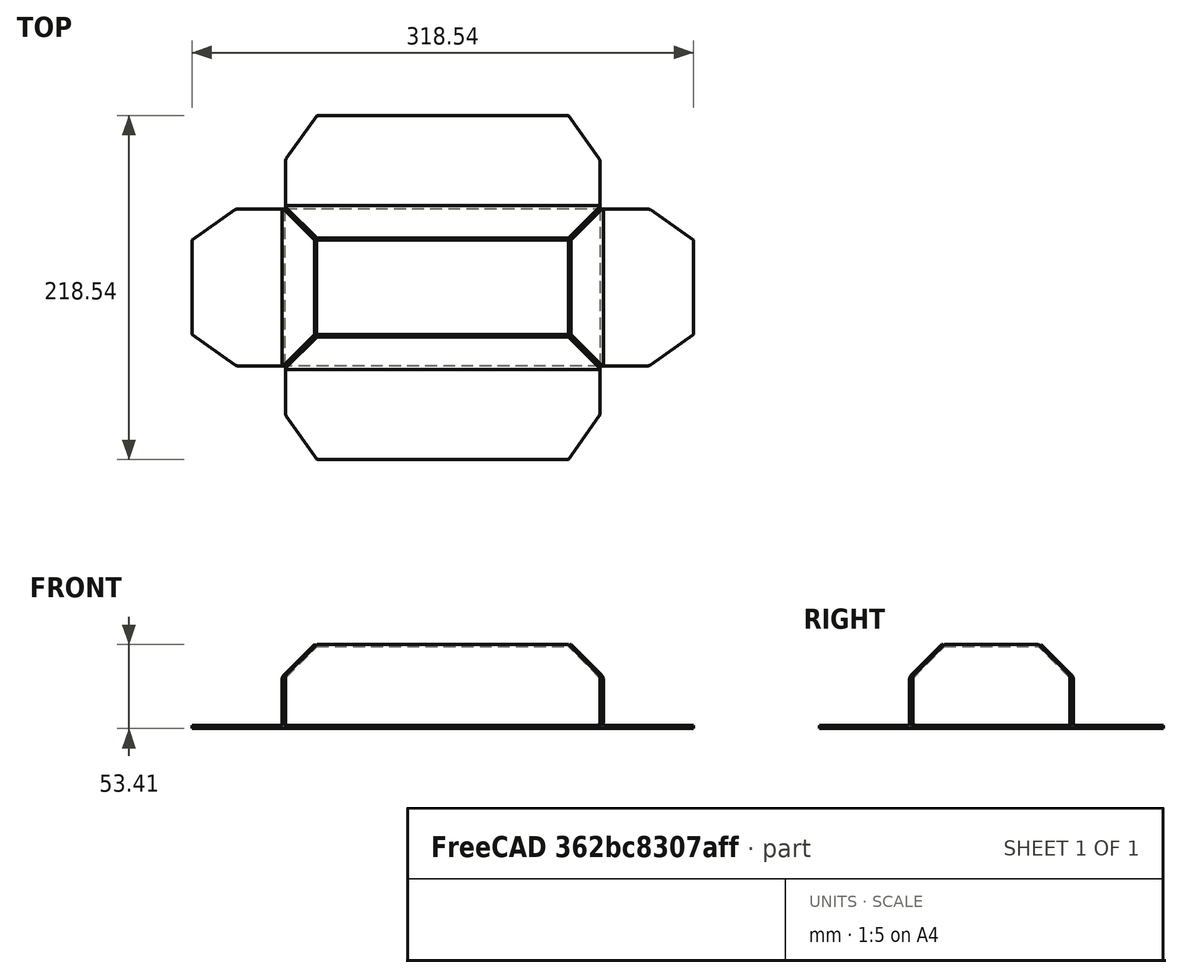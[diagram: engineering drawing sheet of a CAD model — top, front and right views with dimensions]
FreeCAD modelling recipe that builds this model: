
FCSTD DOCUMENT  (FreeCAD 0.19R20996 (Git))
Label: Corner-Rip-02
License: All rights reserved
LicenseURL: www.visualprojections.com.au
objects: Sketcher::SketchObject×2, PartDesign::Fillet×2, PartDesign::Pad×1, PartDesign::Chamfer×1, PartDesign::Body×1, Part::FeaturePython×1, Part::Offset×1, Part::Feature×1
note: 14 computed .brp shape members not serialized (recipe doc carries the construction recipe); baked Part::Feature solids carry a one-line shape summary decoded from their .brp

FEATURE [Sketcher::SketchObject] Sketch
  MapMode = 5
  Support = -> [XY_Plane]
  sketch-geometry (4):
    g0: LineSegment StartX=-100 StartY=50 StartZ=0 EndX=100 EndY=50 EndZ=0
    g1: LineSegment StartX=100 StartY=50 StartZ=0 EndX=100 EndY=-50 EndZ=0
    g2: LineSegment StartX=100 StartY=-50 StartZ=0 EndX=-100 EndY=-50 EndZ=0
    g3: LineSegment StartX=-100 StartY=-50 StartZ=0 EndX=-100 EndY=50 EndZ=0
  constraints (11):
    c: Coincident(g0,g1)
    c: Coincident(g1,g2)
    c: Coincident(g2,g3)
    c: Coincident(g3,g0)
    c: Horizontal(g0)
    c: Horizontal(g2)
    c: Vertical(g1)
    c: Vertical(g3)
    c: Symmetric(g0,g1,g-1)
    c: DistanceX(g0,g0) = 200
    c: DistanceY(g1,g1) = 100
FEATURE [PartDesign::Pad] Pad  label="Inside-Dimensions-of-Part"
  Length = 50
  Length2 = 100
  Profile = -> Sketch
  Type = 0
FEATURE [PartDesign::Chamfer] Chamfer  label="45deg-Angle-Fold"
  Base = -> Pad [Edge10,Edge12,Edge4,Edge7]
  BaseFeature = -> Pad
  Size = 20
  SupportTransform = true
FEATURE [PartDesign::Fillet] Fillet  label="Inside-Radius-of-Part"
  Base = -> Chamfer [Edge15,Edge13,Edge11,Edge12,Edge6,Edge2,Edge3,Edge7]
  BaseFeature = -> Chamfer
  Radius = 2
  SupportTransform = true
FEATURE [PartDesign::Fillet] Fillet001  label="Corner-Relief"
  Base = -> Fillet [Edge28,Edge30,Edge35,Edge32]
  BaseFeature = -> Fillet
  Radius = 0.1
  SupportTransform = true
FEATURE [PartDesign::Body] Body
  Group = -> [Sketch,Pad,Chamfer,Fillet,Fillet001]
  Origin = -> Origin
  Tip = -> Fillet001
FEATURE [Part::FeaturePython] Facebinder  # WARN: FeaturePython — macro-defined, semantics opaque (R4)
  Extrusion = 0
  Faces = -> [Fillet001]
  RemoveSplitter = false
  Sew = false
FEATURE [Part::Offset] Offset
  Fill = true
  Intersection = false
  Join = 0
  Mode = 0
  SelfIntersection = false
  Source = -> Facebinder
  Value = 2
FEATURE [Part::Feature] Unfold
  shape: bbox 318.5 x 218.5 x 2.201 mm, 38 faces (baked)
FEATURE [Sketcher::SketchObject] Sketch001  label="Unfold_Sketch"
  sketch-geometry (84):
    g0: LineSegment StartX=131.816 StartY=-49.3435 StartZ=0 EndX=159.272 EndY=-29.9293 EndZ=0
    g1: LineSegment StartX=159.272 StartY=29.9293 StartZ=0 EndX=159.272 EndY=-29.9293 EndZ=0
    g2: LineSegment StartX=131.816 StartY=49.3435 StartZ=0 EndX=159.272 EndY=29.9293 EndZ=0
    g3: BSplineCurve PolesCount=15 KnotsCount=13 Degree=3 IsPeriodic=0
    g4: BSplineCurve PolesCount=15 KnotsCount=13 Degree=3 IsPeriodic=0
    g5: BSplineCurve PolesCount=15 KnotsCount=13 Degree=3 IsPeriodic=0
    g6: BSplineCurve PolesCount=15 KnotsCount=13 Degree=3 IsPeriodic=0
    g7: BSplineCurve PolesCount=15 KnotsCount=13 Degree=3 IsPeriodic=0
    g8: BSplineCurve PolesCount=15 KnotsCount=13 Degree=3 IsPeriodic=0
    g9: LineSegment StartX=102.43 StartY=49.9 StartZ=0 EndX=129.601 EndY=49.9 EndZ=0
    g10: LineSegment StartX=102.43 StartY=-49.9 StartZ=0 EndX=129.601 EndY=-49.9 EndZ=0
    g11: BSplineCurve PolesCount=15 KnotsCount=13 Degree=3 IsPeriodic=0
    g12: BSplineCurve PolesCount=15 KnotsCount=13 Degree=3 IsPeriodic=0
    g13: BSplineCurve PolesCount=15 KnotsCount=13 Degree=3 IsPeriodic=0
    g14: BSplineCurve PolesCount=15 KnotsCount=13 Degree=3 IsPeriodic=0
    g15: LineSegment StartX=99.3435 StartY=81.816 StartZ=0 EndX=79.9293 EndY=109.272 EndZ=0
    g16: LineSegment StartX=-79.9293 StartY=109.272 StartZ=0 EndX=79.9293 EndY=109.272 EndZ=0
    g17: LineSegment StartX=-99.3435 StartY=81.816 StartZ=0 EndX=-79.9293 EndY=109.272 EndZ=0
    g18: BSplineCurve PolesCount=15 KnotsCount=13 Degree=3 IsPeriodic=0
    g19: BSplineCurve PolesCount=15 KnotsCount=13 Degree=3 IsPeriodic=0
    g20: BSplineCurve PolesCount=15 KnotsCount=13 Degree=3 IsPeriodic=0
    g21: BSplineCurve PolesCount=15 KnotsCount=13 Degree=3 IsPeriodic=0
    g22: BSplineCurve PolesCount=15 KnotsCount=13 Degree=3 IsPeriodic=0
    g23: BSplineCurve PolesCount=15 KnotsCount=13 Degree=3 IsPeriodic=0
    g24: LineSegment StartX=-99.9 StartY=52.4296 StartZ=0 EndX=-99.9 EndY=79.6012 EndZ=0
    g25: LineSegment StartX=99.9 StartY=52.4296 StartZ=0 EndX=99.9 EndY=79.6012 EndZ=0
    g26: BSplineCurve PolesCount=15 KnotsCount=13 Degree=3 IsPeriodic=0
    g27: BSplineCurve PolesCount=15 KnotsCount=13 Degree=3 IsPeriodic=0
    g28: BSplineCurve PolesCount=15 KnotsCount=13 Degree=3 IsPeriodic=0
    g29: BSplineCurve PolesCount=15 KnotsCount=13 Degree=3 IsPeriodic=0
    g30: BSplineCurve PolesCount=15 KnotsCount=13 Degree=3 IsPeriodic=0
    g31: BSplineCurve PolesCount=15 KnotsCount=13 Degree=3 IsPeriodic=0
    g32: BSplineCurve PolesCount=15 KnotsCount=13 Degree=3 IsPeriodic=0
    g33: BSplineCurve PolesCount=15 KnotsCount=13 Degree=3 IsPeriodic=0
    g34: BSplineCurve PolesCount=15 KnotsCount=13 Degree=3 IsPeriodic=0
    g35: BSplineCurve PolesCount=15 KnotsCount=13 Degree=3 IsPeriodic=0
    g36: BSplineCurve PolesCount=15 KnotsCount=13 Degree=3 IsPeriodic=0
    g37: BSplineCurve PolesCount=15 KnotsCount=13 Degree=3 IsPeriodic=0
    g38: LineSegment StartX=-99.3435 StartY=-81.816 StartZ=0 EndX=-79.9293 EndY=-109.272 EndZ=0
    g39: LineSegment StartX=79.9293 StartY=-109.272 StartZ=0 EndX=-79.9293 EndY=-109.272 EndZ=0
    g40: LineSegment StartX=99.3435 StartY=-81.816 StartZ=0 EndX=79.9293 EndY=-109.272 EndZ=0
    g41: BSplineCurve PolesCount=15 KnotsCount=13 Degree=3 IsPeriodic=0
    g42: BSplineCurve PolesCount=15 KnotsCount=13 Degree=3 IsPeriodic=0
    g43: BSplineCurve PolesCount=15 KnotsCount=13 Degree=3 IsPeriodic=0
    g44: BSplineCurve PolesCount=15 KnotsCount=13 Degree=3 IsPeriodic=0
    g45: BSplineCurve PolesCount=15 KnotsCount=13 Degree=3 IsPeriodic=0
    g46: BSplineCurve PolesCount=15 KnotsCount=13 Degree=3 IsPeriodic=0
    g47: LineSegment StartX=99.9 StartY=-52.4296 StartZ=0 EndX=99.9 EndY=-79.6012 EndZ=0
    g48: LineSegment StartX=-99.9 StartY=-52.4296 StartZ=0 EndX=-99.9 EndY=-79.6012 EndZ=0
    g49: BSplineCurve PolesCount=15 KnotsCount=13 Degree=3 IsPeriodic=0
    g50: BSplineCurve PolesCount=15 KnotsCount=13 Degree=3 IsPeriodic=0
    g51: BSplineCurve PolesCount=15 KnotsCount=13 Degree=3 IsPeriodic=0
    g52: BSplineCurve PolesCount=15 KnotsCount=13 Degree=3 IsPeriodic=0
    g53: BSplineCurve PolesCount=15 KnotsCount=13 Degree=3 IsPeriodic=0
    g54: BSplineCurve PolesCount=15 KnotsCount=13 Degree=3 IsPeriodic=0
    g55: BSplineCurve PolesCount=15 KnotsCount=13 Degree=3 IsPeriodic=0
    g56: BSplineCurve PolesCount=15 KnotsCount=13 Degree=3 IsPeriodic=0
    g57: LineSegment StartX=-131.816 StartY=49.3435 StartZ=0 EndX=-159.272 EndY=29.9293 EndZ=0
    g58: LineSegment StartX=-159.272 StartY=-29.9293 StartZ=0 EndX=-159.272 EndY=29.9293 EndZ=0
    g59: LineSegment StartX=-131.816 StartY=-49.3435 StartZ=0 EndX=-159.272 EndY=-29.9293 EndZ=0
    g60: BSplineCurve PolesCount=15 KnotsCount=13 Degree=3 IsPeriodic=0
    g61: BSplineCurve PolesCount=15 KnotsCount=13 Degree=3 IsPeriodic=0
    g62: BSplineCurve PolesCount=15 KnotsCount=13 Degree=3 IsPeriodic=0
    g63: BSplineCurve PolesCount=15 KnotsCount=13 Degree=3 IsPeriodic=0
    g64: BSplineCurve PolesCount=15 KnotsCount=13 Degree=3 IsPeriodic=0
    g65: BSplineCurve PolesCount=15 KnotsCount=13 Degree=3 IsPeriodic=0
    g66: LineSegment StartX=-102.43 StartY=-49.9 StartZ=0 EndX=-129.601 EndY=-49.9 EndZ=0
    g67: LineSegment StartX=-102.43 StartY=49.9 StartZ=0 EndX=-129.601 EndY=49.9 EndZ=0
    g68: BSplineCurve PolesCount=15 KnotsCount=13 Degree=3 IsPeriodic=0
    g69: BSplineCurve PolesCount=15 KnotsCount=13 Degree=3 IsPeriodic=0
    g70: BSplineCurve PolesCount=15 KnotsCount=13 Degree=3 IsPeriodic=0
    g71: BSplineCurve PolesCount=15 KnotsCount=13 Degree=3 IsPeriodic=0
    g72: BSplineCurve PolesCount=15 KnotsCount=13 Degree=3 IsPeriodic=0
    g73: BSplineCurve PolesCount=15 KnotsCount=13 Degree=3 IsPeriodic=0
    g74: BSplineCurve PolesCount=15 KnotsCount=13 Degree=3 IsPeriodic=0
    g75: BSplineCurve PolesCount=15 KnotsCount=13 Degree=3 IsPeriodic=0
    g76: LineSegment StartX=130.709 StartY=49.7554 StartZ=0 EndX=130.709 EndY=-49.7554 EndZ=0
    g77: LineSegment StartX=100.215 StartY=49.3435 StartZ=0 EndX=100.215 EndY=-49.3435 EndZ=0
    g78: LineSegment StartX=-99.7554 StartY=80.7086 StartZ=0 EndX=99.7554 EndY=80.7086 EndZ=0
    g79: LineSegment StartX=-99.3435 StartY=50.2148 StartZ=0 EndX=99.3435 EndY=50.2148 EndZ=0
    g80: LineSegment StartX=99.7554 StartY=-80.7086 StartZ=0 EndX=-99.7554 EndY=-80.7086 EndZ=0
    g81: LineSegment StartX=99.3435 StartY=-50.2148 StartZ=0 EndX=-99.3435 EndY=-50.2148 EndZ=0
    g82: LineSegment StartX=-130.709 StartY=-49.7554 StartZ=0 EndX=-130.709 EndY=49.7554 EndZ=0
    g83: LineSegment StartX=-100.215 StartY=-49.3435 StartZ=0 EndX=-100.215 EndY=49.3435 EndZ=0
